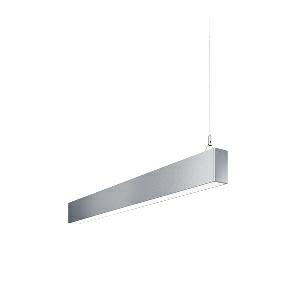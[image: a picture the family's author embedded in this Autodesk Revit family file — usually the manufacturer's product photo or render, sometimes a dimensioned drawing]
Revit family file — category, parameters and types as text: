
# Revit family: idoo_line_-_ilp_2000_830_d_end_00805719_7db0
name_source: partatom
category: Lighting Fixtures
units: mm (PartAtom-declared; Revit-internal decimal feet)

## family parameters
Cut with Voids When Loaded = No
Host = Face
Light Source = No
Part Type = Normal
Room Calculation Point = No
Round Connector Dimension = Use Diameter
Shared = No

## types (1)
- IDOO.line - ILP 2000/830/D END (1 x LED, 2250 lm, 3000K)
    Apparent Load = 17 VA
    Approval mark = CE
    CIE Flux Codes = 66 91 98 40 100
    Color Rendering = 80-89
    Color Temperature = 3000K
    Control Gear = Electronic ballast
    Default Elevation = 1800 mm
    Description = ILP 2000/830/D|Suspended luminaire|light source: LED|connected load: 220-240 V, 50/60 Hz|Power consumption: approx. 17 W|standby: approx. 0,20|luminous flux: 2250 lm|luminous efficacy: 132 lm/W|light distribution: Direct/indirect|direct ratio: approx. 40 %|colour temperature: Warm white, ca. 3000 K|color rendering index (CRI): >= 80|chromaticity tolerance:  3 SDCM|System of protection: IP 40|technology: Continuously dimmable|luminaire body|material: Sectional aluminium|colour: Silver|lamp cover: Acrylic (PMMA), Clear|mains lead: 1,0 m With free stranded wires|Fastening: Steel cable 0.3 - 0.7 m|glare control: Prism aperture|luminance(L65): <= 2700 cd/m|unified glare rating(4H 8H): <=  16|special features: DALI Load 1x, TouchDIM - dimming via standard switch, Through-wired, up to 18 m on one mains connection, Flicker-free, Suitable as emergency lighting, Mechanical and electrical connection of the individual modules without tools|
    Frequency = 50 Hz
    Height = 110 mm
    Lamp = 1 x LED
    Lamp Light Flux = 2250 lm
    Lamp count = 1
    Length = 848 mm
    Luminous efficacy = 132 lm/W
    Manufacturer = Waldmann
    ModVariant = No
    Model = 00805719
    Mounting Place = Ceiling
    Mounting Type = Pendant
    Number of Poles = 1
    OnlyDefault = Yes
    Power Factor = 1
    Product Name = IDOO.line - ILP 2000/830/D END
    Product group = Suspended luminaire
    ProductGroupID = 9
    Protection Class = Protection class I
    Protection Degree = IP 40
    RLX_Detail_Level = 1
    RLX_Emergency_Light_Flux = 0 lm
    RLX_Emergency_Type = 0
    RLX_Emergency_Type_DB = No
    RlxData = <blob elided: 18533 chars, md5=8614ade2>
    Socket = socket
    Standby Power = 0 W
    System Light Flux = 2250 lm
    System Power = 17 W
    Type Comments = Product without accessories
    Type Image = 113300000-00692564.jpg
    URL = http://relux.com
    VarID = ---
    Voltage = 230 V
    Voltage Range = 220-240 V
    Weight = 0.00 kg
    Width = 60 mm  [stored 0.19685 ft]

note: [stored X ft] marks values corroborated as IEEE doubles in the binary element streams (Revit-internal decimal feet)

## geometry (parser evidence)
native form markers: Blend x4, Sweep x14
no freeform markers — native parametric forms only
